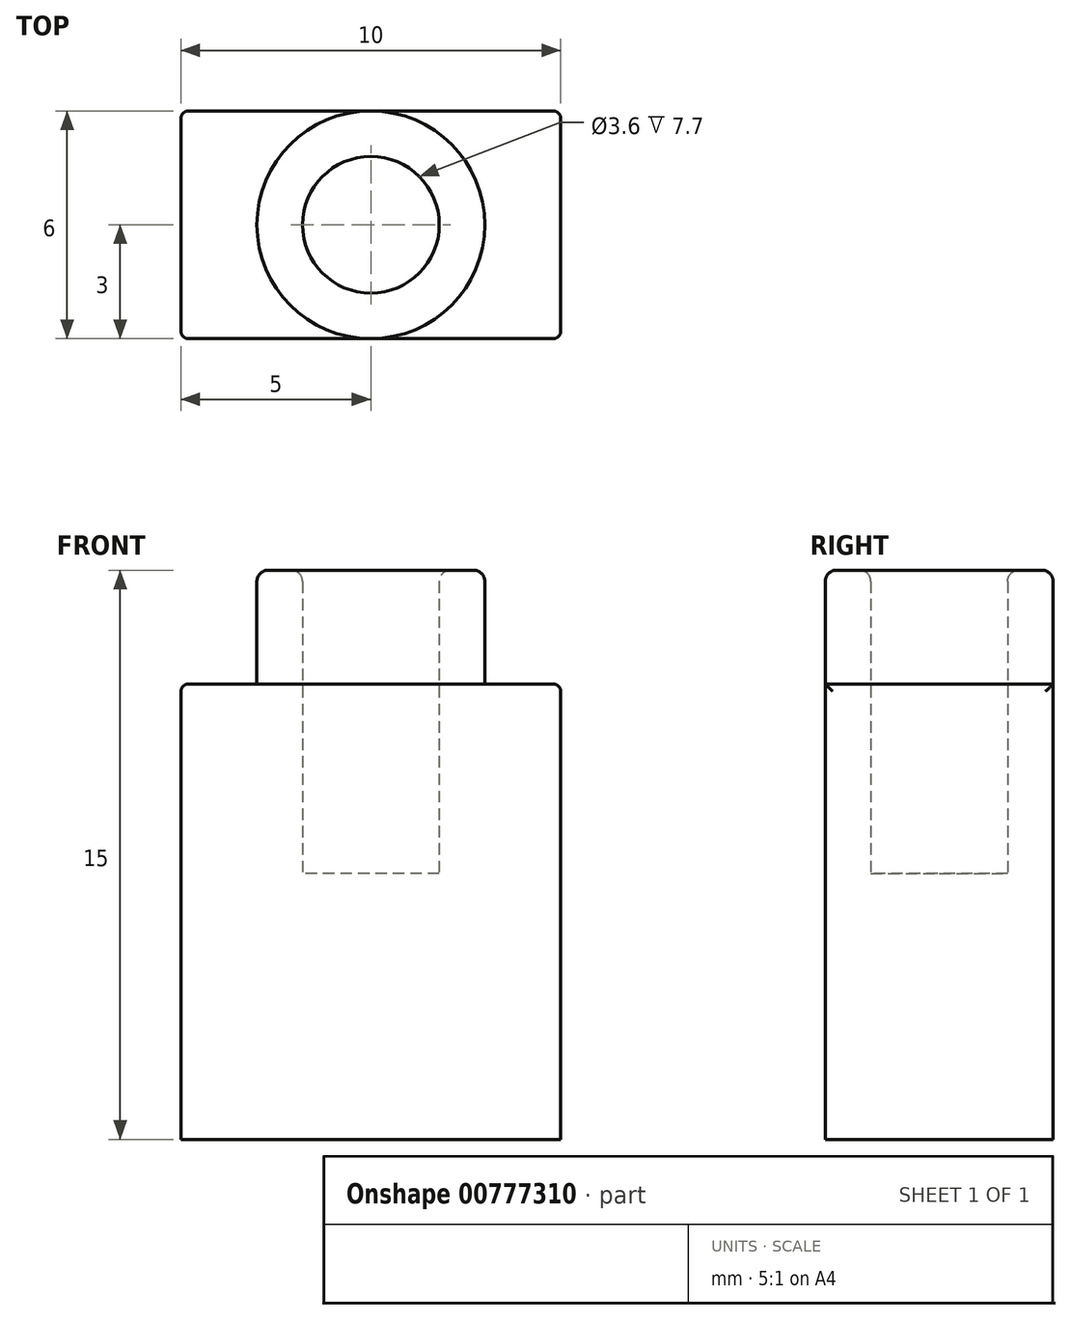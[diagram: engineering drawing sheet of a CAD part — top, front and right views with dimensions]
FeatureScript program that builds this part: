
annotation { "Feature Type Name" : "Feature", "Feature Type Description" : "" }
export const myFeature = defineFeature(function(context is Context, id is Id, definition is map)
    precondition{}
    {
        {
            var Q0;
            Q0=qCreatedBy(makeId("Top.planeOp"),FACE);
            var sketch = newSketch(context, id + "F0", { "sketchPlane" : qUnion([Q0])});
            skLineSegment(sketch, "E0.bottom", {"start": v(-5, 3) * mm, "end": v(5, 3) * mm});
            skLineSegment(sketch, "E0.top", {"start": v(-5, -3) * mm, "end": v(5, -3) * mm});
            skLineSegment(sketch, "E0.left", {"start": v(-5, 3) * mm, "end": v(-5, -3) * mm});
            skLineSegment(sketch, "E0.right", {"start": v(5, 3) * mm, "end": v(5, -3) * mm});
            skPoint(sketch, "E0.middle", {"position": v(0, 0) * mm});
            skCircle(sketch, "E1", {"center": v(0, 0) * mm, "radius": 3 * mm});
            skCircle(sketch, "E2", {"center": v(0, 0) * mm, "radius": 1.8 * mm});
            skSolve(sketch);
        }
        {
            var Q0;
            {var subQ0=sQuery(id+"F0.wireOp",EDGE,"E0.right");Q0=makeQuery(id+"F0.imprint","IMPRINT",FACE,{"disambiguationData":[TD([[makeQuery(id+"F0.imprint","IMPRINT",EDGE,{"derivedFrom":subQ0}),-1.0]])]});}
            var Q1;
            Q1=makeQuery(id+"F0.imprint","IMPRINT",FACE,{"disambiguationData":[TD([[makeQuery(id+"F0.imprint","IMPRINT",EDGE,{"derivedFrom":sQuery(id+"F0.wireOp",EDGE,"E2")}),-1.0]])]});
            var Q2;
            {var subQ0=sQuery(id+"F0.wireOp",EDGE,"E0.left");Q2=makeQuery(id+"F0.imprint","IMPRINT",FACE,{"disambiguationData":[TD([[makeQuery(id+"F0.imprint","IMPRINT",EDGE,{"derivedFrom":subQ0}),1.0]])]});}
            var Q3;
            Q3=makeQuery(id+"F0.imprint","IMPRINT",FACE,{"disambiguationData":[TD([[makeQuery(id+"F0.imprint","IMPRINT",EDGE,{"derivedFrom":sQuery(id+"F0.wireOp",EDGE,"E2")}),1.0]])]});
            extrude(context, id + "F1", {"entities" : qUnion([Q0, Q1, Q2, Q3]), "oppositeDirection" : true, "depth" : 12 * mm, "offsetDistance" : 25 * mm});
        }
        {
            var Q0;
            Q0=makeQuery(id+"F0.imprint","IMPRINT",FACE,{"disambiguationData":[TD([[makeQuery(id+"F0.imprint","IMPRINT",EDGE,{"derivedFrom":sQuery(id+"F0.wireOp",EDGE,"E2")}),-1.0]])]});
            extrude(context, id + "F2", {"entities" : qUnion([Q0]), "operationType" : NewBodyOperationType.ADD, "depth" : 3 * mm, "offsetDistance" : 25 * mm});
        }
        {
            var Q0;
            Q0=makeQuery(id+"F1.opExtrude","SWEPT_EDGE",EDGE,{"disambiguationData":[OSD([sQuery(id+"F0.wireOp",EDGE,"E0.top"),sQuery(id+"F0.wireOp",EDGE,"E0.right")])]});
            var Q1;
            Q1=makeQuery(id+"F1.opExtrude","SWEPT_EDGE",EDGE,{"disambiguationData":[OSD([sQuery(id+"F0.wireOp",EDGE,"E0.bottom"),sQuery(id+"F0.wireOp",EDGE,"E0.right")])]});
            var Q2;
            Q2=makeQuery(id+"F1.opExtrude","SWEPT_EDGE",EDGE,{"disambiguationData":[OSD([sQuery(id+"F0.wireOp",EDGE,"E0.top"),sQuery(id+"F0.wireOp",EDGE,"E0.left")])]});
            var Q3;
            Q3=makeQuery(id+"F1.opExtrude","SWEPT_EDGE",EDGE,{"disambiguationData":[OSD([sQuery(id+"F0.wireOp",EDGE,"E0.bottom"),sQuery(id+"F0.wireOp",EDGE,"E0.left")])]});
            var Q4;
            Q4=makeQuery(id+"F1.opExtrude","CAP_EDGE",EDGE,{"disambiguationData":[OSD([sQuery(id+"F0.wireOp",EDGE,"E0.left")])],"isStart":true});
            var Q5;
            Q5=makeQuery(id+"F1.opExtrude","CAP_EDGE",EDGE,{"disambiguationData":[OSD([sQuery(id+"F0.wireOp",EDGE,"E0.right")])],"isStart":true});
            fillet(context, id + "F3", {"entities" : qUnion([Q0, Q1, Q2, Q3, Q4, Q5]), "radius" : 0.2 * mm, "tangentPropagation" : true, "allowEdgeOverflow" : false});
        }
        {
            var Q0;
            Q0=makeQuery(id+"F2.opExtrude","CAP_EDGE",EDGE,{"disambiguationData":[OSD([sQuery(id+"F0.wireOp",EDGE,"E1")])],"isStart":false});
            var Q1;
            Q1=makeQuery(id+"F2.opExtrude","CAP_EDGE",EDGE,{"disambiguationData":[OSD([sQuery(id+"F0.wireOp",EDGE,"E2")])],"isStart":false});
            fillet(context, id + "F4", {"entities" : qUnion([Q0, Q1]), "radius" : 0.3 * mm, "tangentPropagation" : true, "allowEdgeOverflow" : false});
        }
        {
            var Q0;
            Q0=makeQuery(id+"F0.imprint","IMPRINT",FACE,{"disambiguationData":[TD([[makeQuery(id+"F0.imprint","IMPRINT",EDGE,{"derivedFrom":sQuery(id+"F0.wireOp",EDGE,"E2")}),1.0]])]});
            extrude(context, id + "F5", {"entities" : qUnion([Q0]), "operationType" : NewBodyOperationType.REMOVE, "oppositeDirection" : true, "depth" : 5 * mm, "offsetDistance" : 25 * mm});
        }
    });
